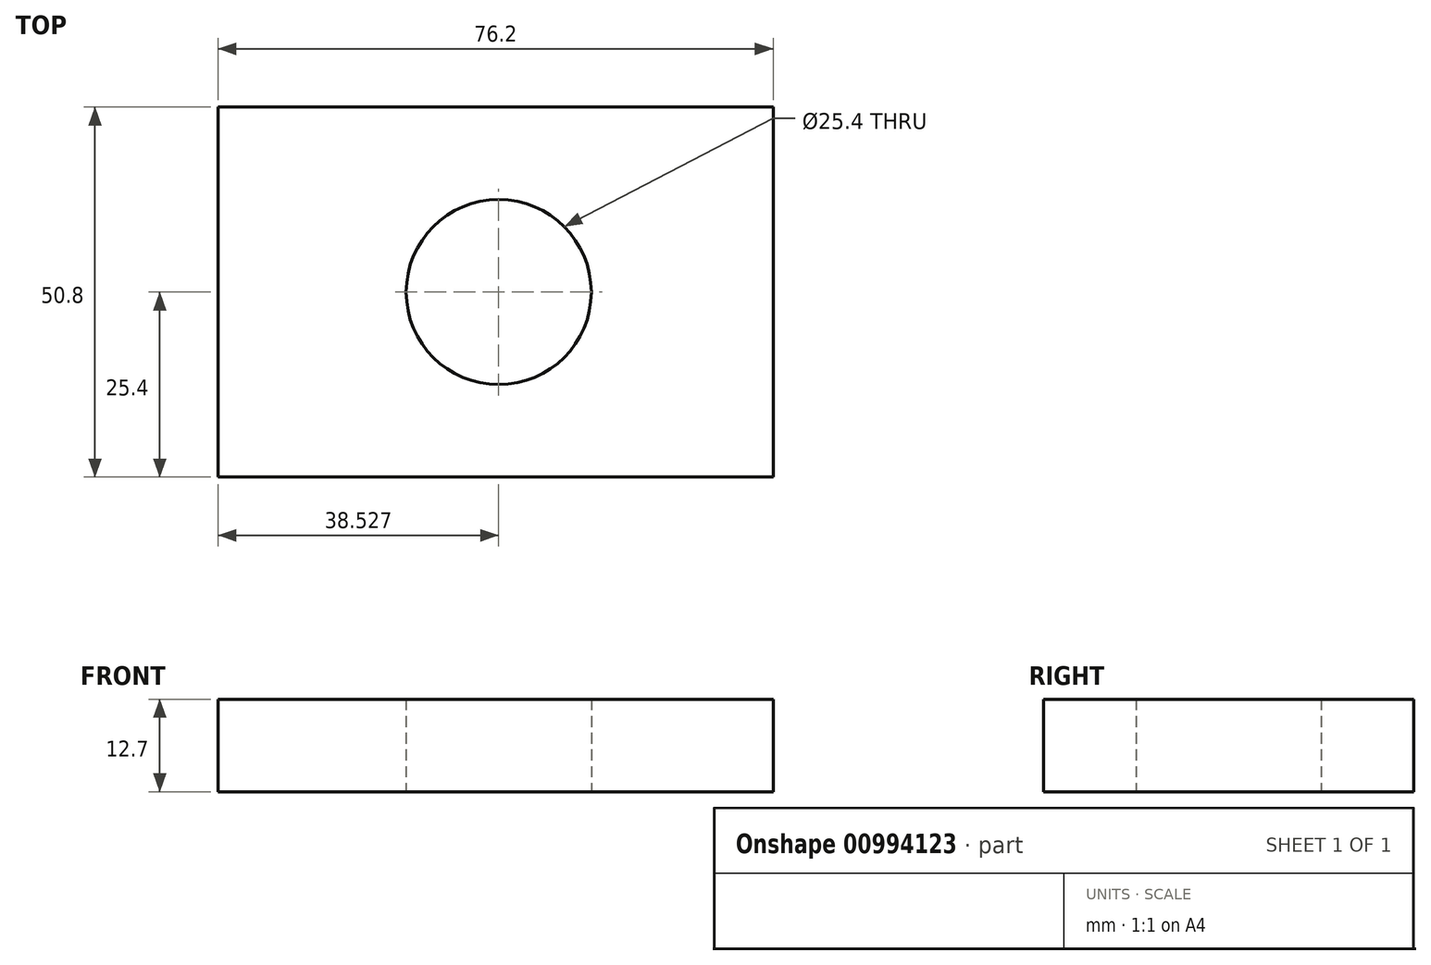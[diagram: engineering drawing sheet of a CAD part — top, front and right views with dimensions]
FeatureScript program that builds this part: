
annotation { "Feature Type Name" : "Feature", "Feature Type Description" : "" }
export const myFeature = defineFeature(function(context is Context, id is Id, definition is map)
    precondition{}
    {
        {
            var Q0;
            Q0=qCreatedBy(makeId("Top.planeOp"),FACE);
            var sketch = newSketch(context, id + "F0", { "sketchPlane" : qUnion([Q0])});
            skLineSegment(sketch, "E0.bottom", {"start": v(38.1, 25.4) * mm, "end": v(-38.1, 25.4) * mm});
            skLineSegment(sketch, "E0.top", {"start": v(38.1, -25.4) * mm, "end": v(-38.1, -25.4) * mm});
            skLineSegment(sketch, "E0.left", {"start": v(38.1, 25.4) * mm, "end": v(38.1, -25.4) * mm});
            skLineSegment(sketch, "E0.right", {"start": v(-38.1, 25.4) * mm, "end": v(-38.1, -25.4) * mm});
            skPoint(sketch, "E0.middle", {"position": v(0, 0) * mm});
            skCircle(sketch, "E1", {"center": v(0.43, 0) * mm, "radius": 12.7 * mm});
            skSolve(sketch);
        }
        {
            var Q0;
            Q0=makeQuery(id+"F0.imprint","IMPRINT",FACE,{"disambiguationData":[TD([[makeQuery(id+"F0.imprint","IMPRINT",EDGE,{"derivedFrom":sQuery(id+"F0.wireOp",EDGE,"E0.bottom")}),1.0]])]});
            var sketch = newSketch(context, id + "F1", { "sketchPlane" : qUnion([Q0])});
            skSolve(sketch);
        }
        {
            var Q0;
            Q0=makeQuery(id+"F1.imprint","IMPRINT",FACE,{"disambiguationData":[TD([[makeQuery(id+"F1.imprint","IMPRINT",EDGE,{"derivedFrom":makeQuery(id+"F0.imprint","IMPRINT",EDGE,{"derivedFrom":sQuery(id+"F0.wireOp",EDGE,"E0.bottom")})}),1.0]])]});
            extrude(context, id + "F2", {"entities" : qUnion([Q0]), "depth" : 12.7 * mm, "offsetDistance" : 25.4 * mm});
        }
    });
